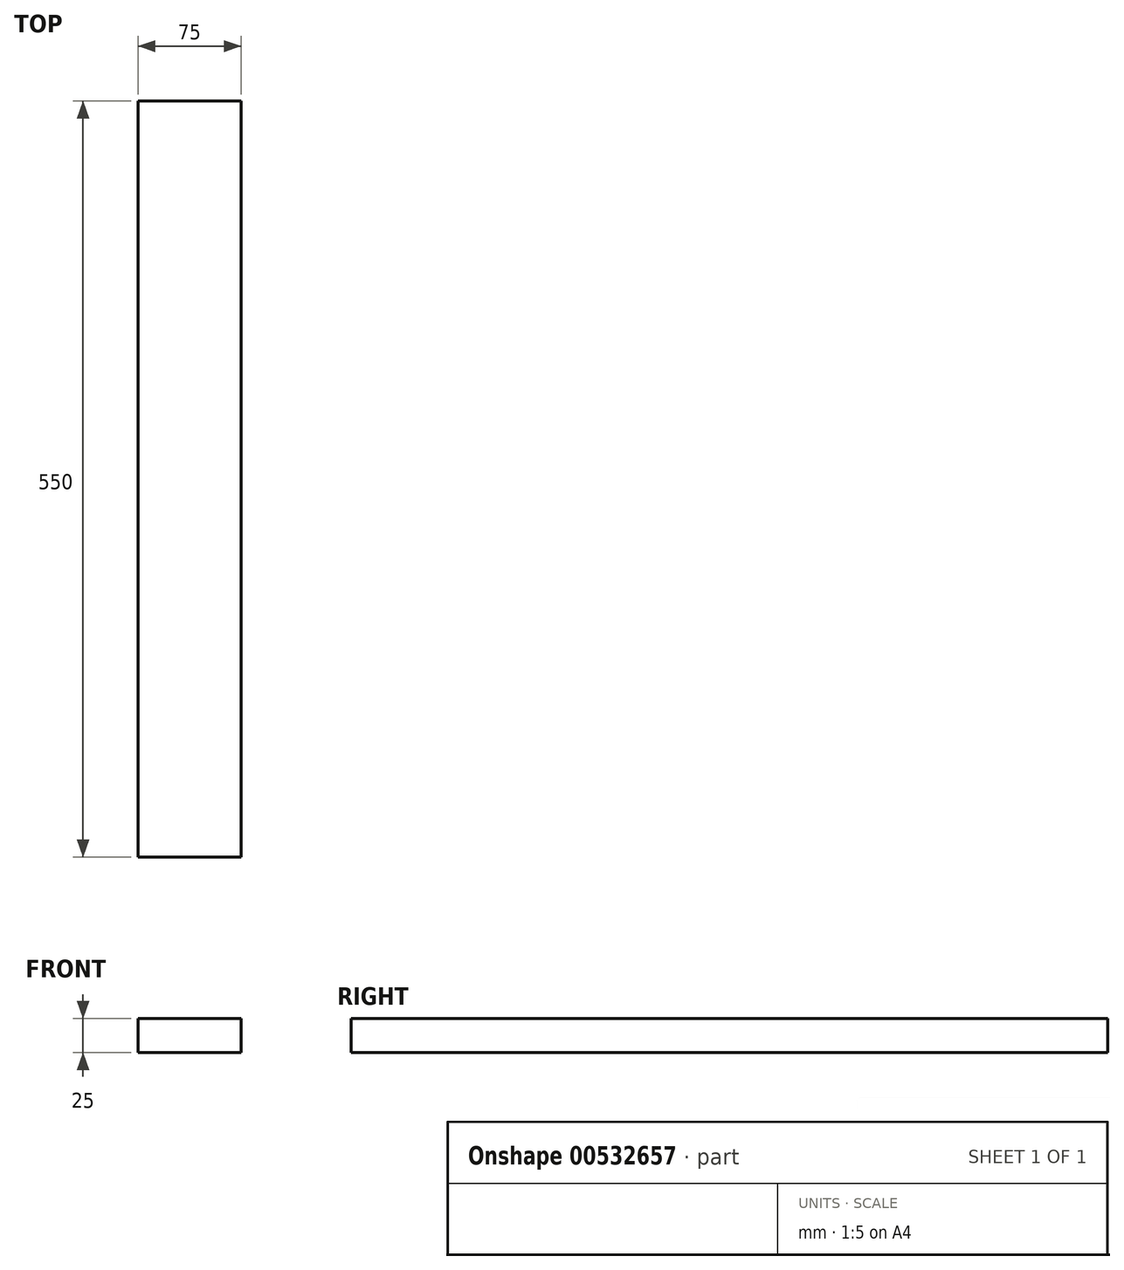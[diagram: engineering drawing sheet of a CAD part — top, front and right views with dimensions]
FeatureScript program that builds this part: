
annotation { "Feature Type Name" : "Feature", "Feature Type Description" : "" }
export const myFeature = defineFeature(function(context is Context, id is Id, definition is map)
    precondition{}
    {
        {
            var Q0;
            Q0=qCreatedBy(makeId("Front.planeOp"),FACE);
            var sketch = newSketch(context, id + "F0", { "sketchPlane" : qUnion([Q0])});
            skLineSegment(sketch, "E0.bottom", {"start": v(-44.2, 4.62) * mm, "end": v(30.8, 4.62) * mm});
            skLineSegment(sketch, "E0.top", {"start": v(-44.2, -20.38) * mm, "end": v(30.8, -20.38) * mm});
            skLineSegment(sketch, "E0.left", {"start": v(-44.2, 4.62) * mm, "end": v(-44.2, -20.38) * mm});
            skLineSegment(sketch, "E0.right", {"start": v(30.8, 4.62) * mm, "end": v(30.8, -20.38) * mm});
            skSolve(sketch);
        }
        {
            var Q0;
            Q0 = qSketchRegion(id + "F0", true);
            extrude(context, id + "F1", {"entities" : qUnion([Q0]), "oppositeDirection" : true, "depth" : 550 * mm, "offsetDistance" : 25 * mm});
        }
    });
